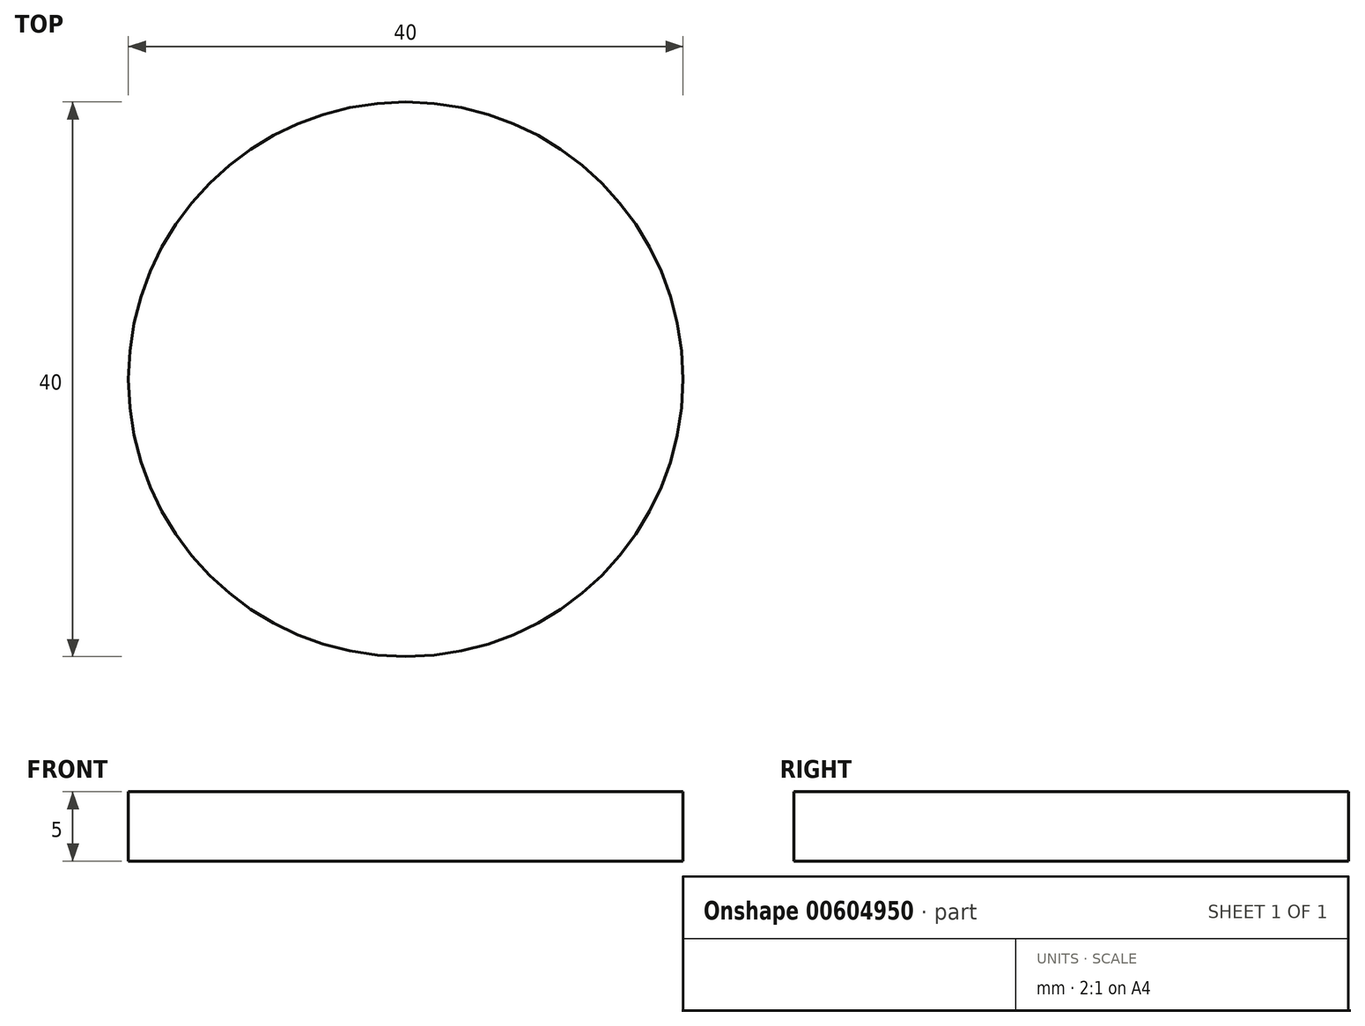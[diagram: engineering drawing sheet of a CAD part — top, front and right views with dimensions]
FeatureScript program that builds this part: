
annotation { "Feature Type Name" : "Feature", "Feature Type Description" : "" }
export const myFeature = defineFeature(function(context is Context, id is Id, definition is map)
    precondition{}
    {
        {
            var Q0;
            Q0=qCreatedBy(makeId("Top.planeOp"),FACE);
            var sketch = newSketch(context, id + "F0", { "sketchPlane" : qUnion([Q0])});
            skCircle(sketch, "E0", {"center": v(0, 0) * mm, "radius": 20 * mm});
            skSolve(sketch);
        }
        {
            var Q0;
            Q0=makeQuery(id+"F0.imprint","IMPRINT",FACE,{"disambiguationData":[TD([[makeQuery(id+"F0.imprint","IMPRINT",EDGE,{"derivedFrom":sQuery(id+"F0.wireOp",EDGE,"E0")}),1.0]])]});
            extrude(context, id + "F1", {"entities" : qUnion([Q0]), "depth" : 5 * mm, "offsetDistance" : 25 * mm});
        }
    });
